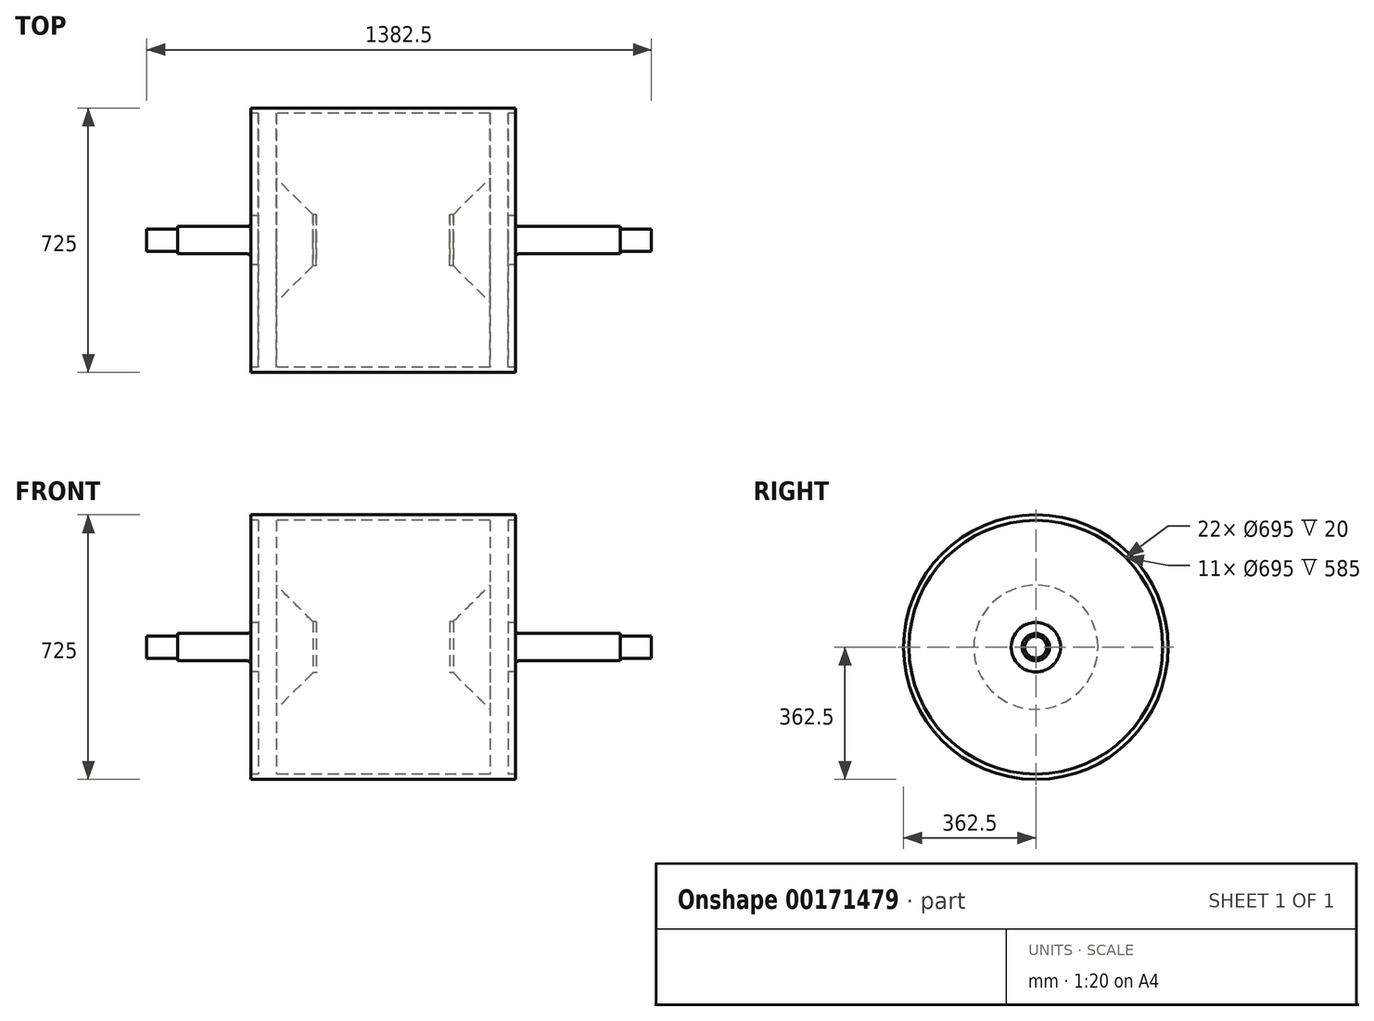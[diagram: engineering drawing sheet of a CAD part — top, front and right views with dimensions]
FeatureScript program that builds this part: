
annotation { "Feature Type Name" : "Feature", "Feature Type Description" : "" }
export const myFeature = defineFeature(function(context is Context, id is Id, definition is map)
    precondition{}
    {
        {
            var Q0;
            Q0=qCreatedBy(makeId("Front.planeOp"),FACE);
            var sketch = newSketch(context, id + "F0", { "sketchPlane" : qUnion([Q0])});
            skLineSegment(sketch, "E0", {"start": v(0, 0) * mm, "end": v(1382.5, 0) * mm, "construction": true});
            skLineSegment(sketch, "E1", {"start": v(0, 0) * mm, "end": v(0, 30) * mm});
            skLineSegment(sketch, "E2", {"start": v(0, 30) * mm, "end": v(85, 30) * mm});
            skLineSegment(sketch, "E3", {"start": v(85, 30) * mm, "end": v(85, 0) * mm});
            skLineSegment(sketch, "E4", {"start": v(85, 30) * mm, "end": v(85, 37.5) * mm});
            skLineSegment(sketch, "E5", {"start": v(85, 37.5) * mm, "end": v(285, 37.5) * mm});
            skLineSegment(sketch, "E6", {"start": v(285, 37.5) * mm, "end": v(285, 0) * mm});
            skLineSegment(sketch, "E7", {"start": v(285, 37.5) * mm, "end": v(285, 50) * mm});
            skLineSegment(sketch, "E8", {"start": v(285, 50) * mm, "end": v(465, 50) * mm});
            skLineSegment(sketch, "E9", {"start": v(285, 50) * mm, "end": v(285, 362.5) * mm, "construction": true});
            skLineSegment(sketch, "E10", {"start": v(285, 362.5) * mm, "end": v(1010, 362.5) * mm});
            skLineSegment(sketch, "E11", {"start": v(1010, 362.5) * mm, "end": v(1010, 347.5) * mm});
            skPoint(sketch, "E12", {"position": v(285, 67.5) * mm});
            skLineSegment(sketch, "E13", {"start": v(285, 67.5) * mm, "end": v(355, 67.5) * mm});
            skLineSegment(sketch, "E14", {"start": v(355, 67.5) * mm, "end": v(355, 50) * mm});
            skLineSegment(sketch, "E15", {"start": v(355, 67.5) * mm, "end": v(355, 70) * mm});
            skLineSegment(sketch, "E16", {"start": v(355, 70) * mm, "end": v(465, 70) * mm});
            skLineSegment(sketch, "E17", {"start": v(465, 50) * mm, "end": v(465, 70) * mm});
            skLineSegment(sketch, "E18", {"start": v(465, 50) * mm, "end": v(465, 0) * mm});
            skPoint(sketch, "E19", {"position": v(285, 347.5) * mm});
            skLineSegment(sketch, "E20", {"start": v(285, 347.5) * mm, "end": v(1010, 347.5) * mm});
            skPoint(sketch, "E21", {"position": v(305, 67.5) * mm});
            skLineSegment(sketch, "E22", {"start": v(305, 67.5) * mm, "end": v(305, 347.5) * mm});
            skLineSegment(sketch, "E23", {"start": v(285, 362.5) * mm, "end": v(285, 347.5) * mm});
            skLineSegment(sketch, "E24", {"start": v(285, 67.5) * mm, "end": v(285, 50) * mm});
            skLineSegment(sketch, "E25", {"start": v(355, 70) * mm, "end": v(355, 347.5) * mm});
            skPoint(sketch, "E26", {"position": v(455, 70) * mm});
            skPoint(sketch, "E27", {"position": v(355, 170) * mm});
            skLineSegment(sketch, "E28", {"start": v(355, 170) * mm, "end": v(455, 70) * mm});
            skLineSegment(sketch, "E29", {"start": v(0, 0) * mm, "end": v(465, 0) * mm});
            skPoint(sketch, "E30", {"position": v(647.5, 0) * mm});
            skPoint(sketch, "E30.positionSnap0", {"position": v(647.5, 347.5) * mm});
            skLineSegment(sketch, "E31", {"start": v(647.5, 347.5) * mm, "end": v(647.5, 0) * mm});
            skLineSegment(sketch, "E32.MirrorCS", {"start": v(990, 67.5) * mm, "end": v(990, 347.5) * mm});
            skLineSegment(sketch, "E33.MirrorCS", {"start": v(940, 70) * mm, "end": v(940, 347.5) * mm});
            skLineSegment(sketch, "E34.MirrorCS", {"start": v(940, 170) * mm, "end": v(840, 70) * mm});
            skLineSegment(sketch, "E35.MirrorCS", {"start": v(940, 70) * mm, "end": v(830, 70) * mm});
            skLineSegment(sketch, "E36.MirrorCS", {"start": v(1010, 50) * mm, "end": v(830, 50) * mm});
            skLineSegment(sketch, "E37.MirrorCS", {"start": v(830, 50) * mm, "end": v(830, 0) * mm});
            skLineSegment(sketch, "E38.MirrorCS", {"start": v(830, 50) * mm, "end": v(830, 70) * mm});
            skLineSegment(sketch, "E39.MirrorCS", {"start": v(1010, 67.5) * mm, "end": v(940, 67.5) * mm});
            skLineSegment(sketch, "E40.MirrorCS", {"start": v(1010, 37.5) * mm, "end": v(1010, 50) * mm});
            skLineSegment(sketch, "E41.MirrorCS", {"start": v(1010, 37.5) * mm, "end": v(1010, 0) * mm});
            skLineSegment(sketch, "E42.MirrorCS", {"start": v(940, 67.5) * mm, "end": v(940, 70) * mm});
            skLineSegment(sketch, "E43.MirrorCS", {"start": v(1010, 50) * mm, "end": v(1010, 362.5) * mm, "construction": true});
            skLineSegment(sketch, "E44", {"start": v(1010, 67.5) * mm, "end": v(1010, 50) * mm});
            skLineSegment(sketch, "E45", {"start": v(830, 0) * mm, "end": v(1010, 0) * mm});
            skLineSegment(sketch, "E46", {"start": v(1010, 0) * mm, "end": v(1297.5, 0) * mm});
            skLineSegment(sketch, "E47", {"start": v(1297.5, 0) * mm, "end": v(1297.5, 37.5) * mm});
            skPoint(sketch, "E47.endSnap0", {"position": v(185, 37.5) * mm});
            skLineSegment(sketch, "E48", {"start": v(1297.5, 37.5) * mm, "end": v(1010, 37.5) * mm});
            skPoint(sketch, "E49", {"position": v(1297.5, 30) * mm});
            skLineSegment(sketch, "E50", {"start": v(1297.5, 30) * mm, "end": v(1382.5, 30) * mm});
            skLineSegment(sketch, "E51", {"start": v(1382.5, 30) * mm, "end": v(1382.5, 0) * mm});
            skLineSegment(sketch, "E52", {"start": v(1297.5, 0) * mm, "end": v(1382.5, 0) * mm});
            skSolve(sketch);
        }
        {
            var Q0;
            Q0=qSketchRegion(id+"F0",true);
            var Q1;
            Q1=sQuery(id+"F0.wireOp",EDGE,"E0");
            revolve(context, id + "F1", {"entities" : qUnion([Q0]), "axis" : qUnion([Q1]), "revolveType" : RevolveType.FULL});
        }
        {
            var Q0;
            Q0=makeQuery(id+"F1.opRevolve","SWEPT_EDGE",EDGE,{"disambiguationData":[OSD([sQuery(id+"F0.wireOp",EDGE,"E41.MirrorCS"),sQuery(id+"F0.wireOp",EDGE,"E40.MirrorCS"),sQuery(id+"F0.wireOp",EDGE,"E48")])]});
            var Q1;
            Q1=makeQuery(id+"F1.opRevolve","SWEPT_EDGE",EDGE,{"disambiguationData":[OSD([sQuery(id+"F0.wireOp",EDGE,"E5"),sQuery(id+"F0.wireOp",EDGE,"E6"),sQuery(id+"F0.wireOp",EDGE,"E7")])]});
            fillet(context, id + "F2", {"entities" : qUnion([Q0, Q1]), "radius" : 10 * mm, "tangentPropagation" : true, "allowEdgeOverflow" : false});
        }
        {
            var Q0;
            Q0=makeQuery(id+"F1.opRevolve","SWEPT_EDGE",EDGE,{"disambiguationData":[OSD([sQuery(id+"F0.wireOp",EDGE,"E2"),sQuery(id+"F0.wireOp",EDGE,"E3"),sQuery(id+"F0.wireOp",EDGE,"E4")])]});
            var Q1;
            Q1=makeQuery(id+"F1.opRevolve","SWEPT_EDGE",EDGE,{"disambiguationData":[OSD([sQuery(id+"F0.wireOp",EDGE,"E47"),sQuery(id+"F0.wireOp",EDGE,"E50")])]});
            fillet(context, id + "F3", {"entities" : qUnion([Q0, Q1]), "radius" : 5 * mm, "tangentPropagation" : true, "allowEdgeOverflow" : false});
        }
        {
            var Q0;
            Q0=makeQuery(id+"F1.opRevolve","SWEPT_FACE",FACE,{"disambiguationData":[OSD([sQuery(id+"F0.wireOp",EDGE,"E11")])]});
            cPlane(context, id + "F4", {"entities" : qUnion([Q0]), "cplaneType" : CPlaneType.OFFSET, "offset" : 75 * mm, "oppositeDirection" : true, "width" : 150 * mm, "height" : 150 * mm});
        }
    });
